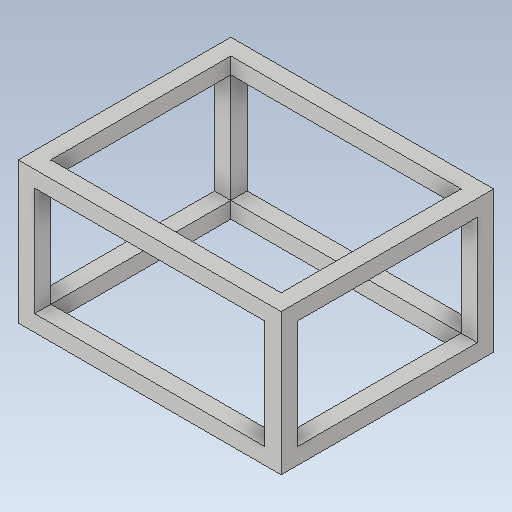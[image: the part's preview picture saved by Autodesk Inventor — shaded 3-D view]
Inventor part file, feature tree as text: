
AUTODESK INVENTOR PART (.ipt)
format: ipt  version: 2020 (Build 240168000, 168)  size: 149,504 bytes
history: native  units: mm
features: extrude x4, sketch x4
ambient origin geometry x8: Origin, YZ Plane, XZ Plane, XY Plane, X Axis, Y Axis, Z Axis, Center Point
bodies: Solid1 (feature_tree)
feature tree (8):
  extrude  "Extrusion1"  Depth=173.35mm
  extrude  "Extrusion2"  Depth=20.0mm
  extrude  "Extrusion3"  Depth=20.0mm
  extrude  "Extrusion4"  Depth=20.0mm TaperAngle=0.0deg
  sketch  "Sketch1"  dims[d0=322.448mm d1=173.35mm]
  sketch  "Sketch2"  dims[d2=260.725mm d3=0.0mm d4=20.0mm]
  sketch  "Sketch3"  dims[d5=20.0mm d6=20.0mm]
  sketch  "Sketch4"  dims[d7=20.0mm d8=900.0mm d9=0.0mm d10=20.0mm d11=20.0mm d12=20.0mm d13=20.0mm d14=900.0mm d15=0.0mm d16=20.0mm d17=20.0mm d18=20.0mm d19=20.0mm d20=900.0mm d21=0.0mm]
